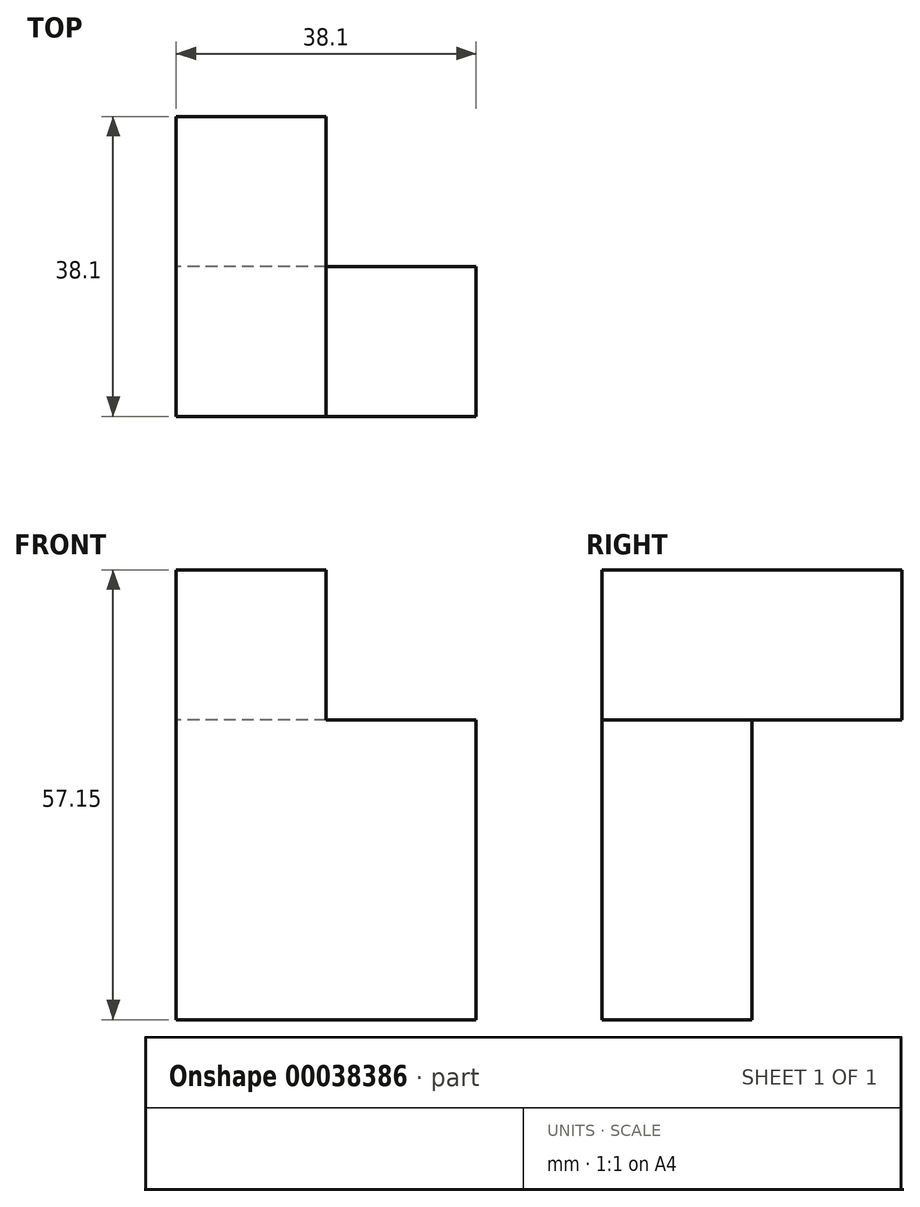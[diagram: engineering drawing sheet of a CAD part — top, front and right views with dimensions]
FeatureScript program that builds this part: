
annotation { "Feature Type Name" : "Feature", "Feature Type Description" : "" }
export const myFeature = defineFeature(function(context is Context, id is Id, definition is map)
    precondition{}
    {
        {
            var Q0;
            Q0=qCreatedBy(makeId("Top.planeOp"),FACE);
            var sketch = newSketch(context, id + "F0", { "sketchPlane" : qUnion([Q0])});
            skLineSegment(sketch, "E0.bottom", {"start": v(0, 0) * mm, "end": v(19.05, 0) * mm});
            skLineSegment(sketch, "E0.top", {"start": v(0, 19.05) * mm, "end": v(19.05, 19.05) * mm});
            skLineSegment(sketch, "E0.left", {"start": v(0, 0) * mm, "end": v(0, 19.05) * mm});
            skLineSegment(sketch, "E0.right", {"start": v(19.05, 0) * mm, "end": v(19.05, 19.05) * mm});
            skSolve(sketch);
        }
        {
            var Q0;
            Q0=makeQuery(id+"F0.imprint","IMPRINT",FACE,{"disambiguationData":[TD([[makeQuery(id+"F0.imprint","IMPRINT",EDGE,{"derivedFrom":sQuery(id+"F0.wireOp",EDGE,"E0.bottom")}),1.0]])]});
            extrude(context, id + "F1", {"entities" : qUnion([Q0]), "depth" : 19.05 * mm});
        }
        {
            var Q0;
            Q0=makeQuery(id+"F1.opExtrude","SWEPT_FACE",FACE,{"disambiguationData":[OSD([sQuery(id+"F0.wireOp",EDGE,"E0.right")])]});
            extrude(context, id + "F2", {"entities" : qUnion([Q0]), "operationType" : NewBodyOperationType.ADD, "depth" : 19.05 * mm});
        }
        {
            var Q0;
            {var subQ0=sQuery(id+"F0.wireOp",EDGE,"E0.right");Q0=makeQuery(id+"F2.boolean.opBoolean","MERGE",FACE,{"derivedFrom":[makeQuery(id+"F1.opExtrude","CAP_FACE",FACE,{"disambiguationData":[OSD([sQuery(id+"F0.wireOp",EDGE,"E0.bottom"),sQuery(id+"F0.wireOp",EDGE,"E0.top"),sQuery(id+"F0.wireOp",EDGE,"E0.left"),subQ0])],"isStart":false}),makeQuery(id+"F2.opExtrude","SWEPT_FACE",FACE,{"disambiguationData":[OSD([subQ0]),TDD([makeQuery(id+"F1.opExtrude","CAP_EDGE",EDGE,{"disambiguationData":[OSD([subQ0])],"isStart":false})])]})]});}
            extrude(context, id + "F3", {"entities" : qUnion([Q0]), "operationType" : NewBodyOperationType.ADD, "depth" : 19.05 * mm});
        }
        {
            var Q0;
            Q0=makeQuery(id+"F3.opExtrude","CAP_FACE",FACE,{"disambiguationData":[OSD([sQuery(id+"F0.wireOp",EDGE,"E0.bottom"),sQuery(id+"F0.wireOp",EDGE,"E0.top"),sQuery(id+"F0.wireOp",EDGE,"E0.left"),sQuery(id+"F0.wireOp",EDGE,"E0.right")])],"isStart":false});
            var sketch = newSketch(context, id + "F4", { "sketchPlane" : qUnion([Q0])});
            skLineSegment(sketch, "E1.bottom", {"start": v(38.1, 0) * mm, "end": v(19.05, 0) * mm});
            skLineSegment(sketch, "E1.top", {"start": v(38.1, 19.05) * mm, "end": v(19.05, 19.05) * mm});
            skLineSegment(sketch, "E1.left", {"start": v(38.1, 0) * mm, "end": v(38.1, 19.05) * mm});
            skLineSegment(sketch, "E1.right", {"start": v(19.05, 0) * mm, "end": v(19.05, 19.05) * mm});
            skLineSegment(sketch, "E2.bottom", {"start": v(19.05, 19.05) * mm, "end": v(0, 19.05) * mm});
            skLineSegment(sketch, "E2.top", {"start": v(19.05, 0) * mm, "end": v(0, 0) * mm});
            skLineSegment(sketch, "E2.left", {"start": v(19.05, 19.05) * mm, "end": v(19.05, 0) * mm});
            skLineSegment(sketch, "E2.right", {"start": v(0, 19.05) * mm, "end": v(0, 0) * mm});
            skSolve(sketch);
        }
        {
            var Q0;
            Q0=makeQuery(id+"F4.imprint","IMPRINT",FACE,{"disambiguationData":[TD([[makeQuery(id+"F4.imprint","IMPRINT",EDGE,{"derivedFrom":sQuery(id+"F4.wireOp",EDGE,"E2.bottom")}),-1.0]])]});
            extrude(context, id + "F5", {"entities" : qUnion([Q0]), "operationType" : NewBodyOperationType.ADD, "depth" : 19.05 * mm});
        }
        {
            var Q0;
            {var subQ0=sQuery(id+"F0.wireOp",EDGE,"E0.top");var subQ1=sQuery(id+"F0.wireOp",EDGE,"E0.right");Q0=makeQuery(id+"F5.boolean.opBoolean","MERGE",FACE,{"derivedFrom":[makeQuery(id+"F3.boolean.opBoolean","MERGE",FACE,{"derivedFrom":[makeQuery(id+"F2.boolean.opBoolean","MERGE",FACE,{"derivedFrom":[makeQuery(id+"F1.opExtrude","SWEPT_FACE",FACE,{"disambiguationData":[OSD([subQ0])]}),makeQuery(id+"F2.opExtrude","SWEPT_FACE",FACE,{"disambiguationData":[OSD([subQ0,subQ1])]})]}),makeQuery(id+"F3.opExtrude","SWEPT_FACE",FACE,{"disambiguationData":[OSD([subQ0,subQ1])]})]}),makeQuery(id+"F5.opExtrude","SWEPT_FACE",FACE,{"disambiguationData":[OSD([sQuery(id+"F4.wireOp",EDGE,"E2.bottom")])]})]});}
            var sketch = newSketch(context, id + "F6", { "sketchPlane" : qUnion([Q0])});
            skLineSegment(sketch, "E3.bottom", {"start": v(-19.05, 57.15) * mm, "end": v(0, 57.15) * mm});
            skLineSegment(sketch, "E3.top", {"start": v(-19.05, 38.1) * mm, "end": v(0, 38.1) * mm});
            skLineSegment(sketch, "E3.left", {"start": v(-19.05, 57.15) * mm, "end": v(-19.05, 38.1) * mm});
            skLineSegment(sketch, "E3.right", {"start": v(0, 57.15) * mm, "end": v(0, 38.1) * mm});
            skLineSegment(sketch, "E4.top", {"start": v(-19.05, 19.54) * mm, "end": v(0, 19.54) * mm});
            skLineSegment(sketch, "E4.left", {"start": v(-19.05, 38.1) * mm, "end": v(-19.05, 19.54) * mm});
            skLineSegment(sketch, "E4.right", {"start": v(0, 38.1) * mm, "end": v(0, 19.54) * mm});
            skLineSegment(sketch, "E5.bottom", {"start": v(0, 19.54) * mm, "end": v(-19.05, 19.54) * mm});
            skLineSegment(sketch, "E5.top", {"start": v(0, 0) * mm, "end": v(-19.05, 0) * mm});
            skLineSegment(sketch, "E5.left", {"start": v(0, 19.54) * mm, "end": v(0, 0) * mm});
            skLineSegment(sketch, "E5.right", {"start": v(-19.05, 19.54) * mm, "end": v(-19.05, 0) * mm});
            skLineSegment(sketch, "E6.bottom", {"start": v(-38.1, 38.1) * mm, "end": v(-19.05, 38.1) * mm});
            skLineSegment(sketch, "E6.top", {"start": v(-38.1, 19.54) * mm, "end": v(-19.05, 19.54) * mm});
            skLineSegment(sketch, "E6.left", {"start": v(-38.1, 38.1) * mm, "end": v(-38.1, 19.54) * mm});
            skLineSegment(sketch, "E7.top", {"start": v(-38.1, 0) * mm, "end": v(-19.05, 0) * mm});
            skLineSegment(sketch, "E7.left", {"start": v(-38.1, 19.54) * mm, "end": v(-38.1, 0) * mm});
            skSolve(sketch);
        }
        {
            var Q0;
            Q0=makeQuery(id+"F6.imprint","IMPRINT",FACE,{"disambiguationData":[TD([[makeQuery(id+"F6.imprint","IMPRINT",EDGE,{"derivedFrom":sQuery(id+"F6.wireOp",EDGE,"E3.bottom")}),1.0]])]});
            extrude(context, id + "F7", {"entities" : qUnion([Q0]), "operationType" : NewBodyOperationType.ADD, "depth" : 19.05 * mm});
        }
    });
